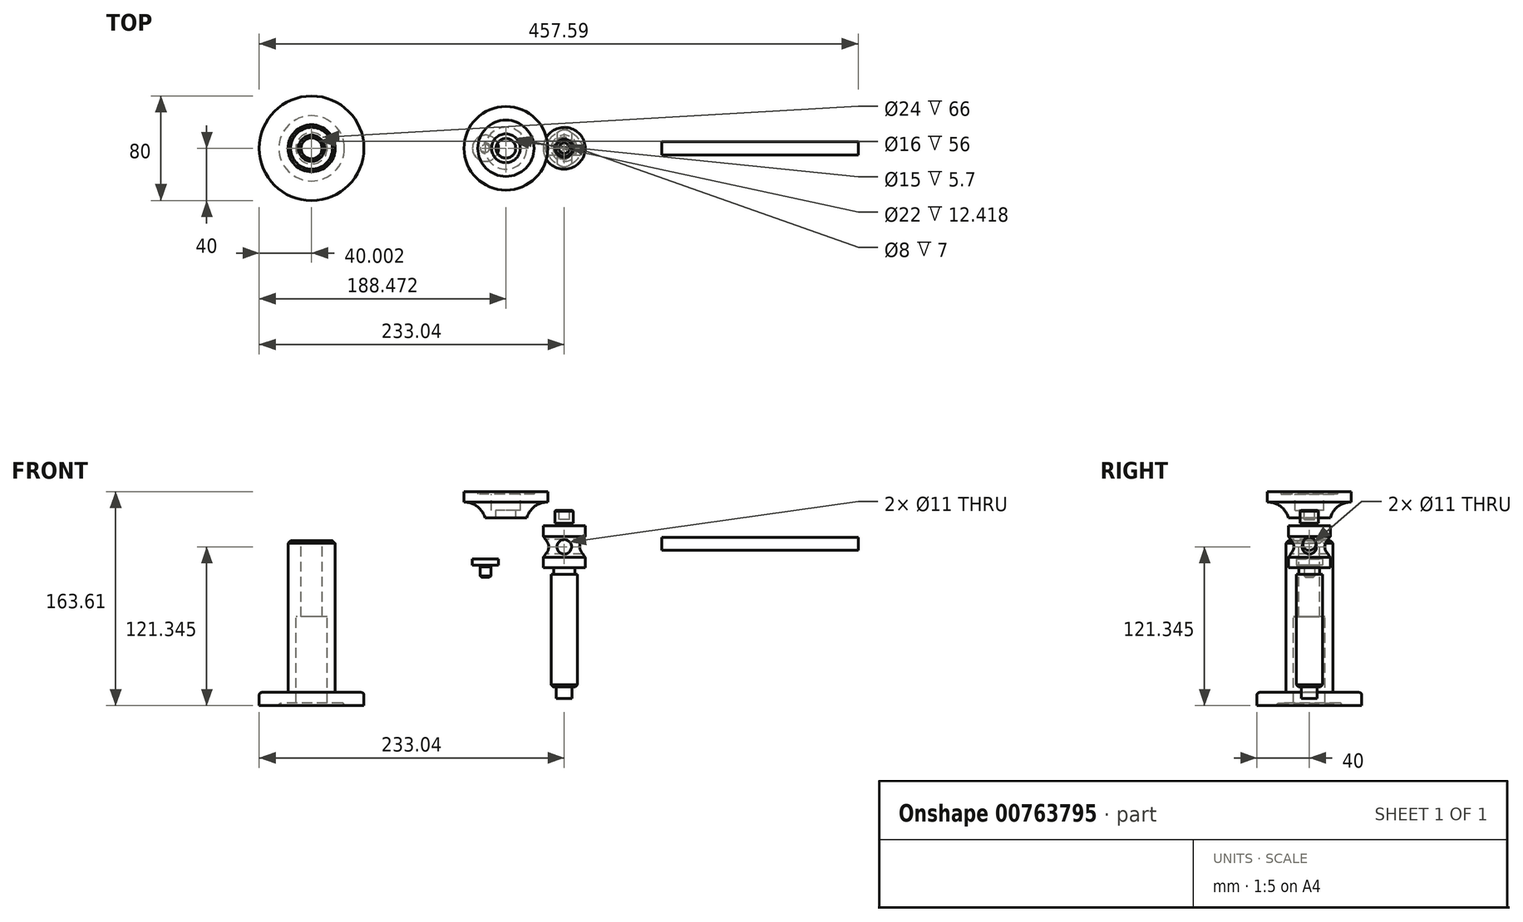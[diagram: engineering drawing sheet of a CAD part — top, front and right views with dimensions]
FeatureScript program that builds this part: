
annotation { "Feature Type Name" : "Feature", "Feature Type Description" : "" }
export const myFeature = defineFeature(function(context is Context, id is Id, definition is map)
    precondition{}
    {
        {
            var Q0;
            Q0=qCreatedBy(makeId("Right.planeOp"),FACE);
            var sketch = newSketch(context, id + "F0", { "sketchPlane" : qUnion([Q0])});
            skLineSegment(sketch, "E0", {"start": v(0, 128.7) * mm, "end": v(0, -124.16) * mm, "construction": true});
            skLineSegment(sketch, "E1", {"start": v(55.08, 81.35) * mm, "end": v(7, 81.35) * mm, "construction": true});
            skLineSegment(sketch, "E2", {"start": v(60.93, -62.65) * mm, "end": v(-52.02, -62.65) * mm, "construction": true});
            skLineSegment(sketch, "E3", {"start": v(58.64, 37.35) * mm, "end": v(-57.7, 37.35) * mm, "construction": true});
            skLineSegment(sketch, "E4", {"start": v(0, -62.65) * mm, "end": v(6, -62.65) * mm});
            skLineSegment(sketch, "E5", {"start": v(6, -62.65) * mm, "end": v(6, -53.65) * mm});
            skLineSegment(sketch, "E6", {"start": v(6, -53.65) * mm, "end": v(8.5, -53.65) * mm});
            skLineSegment(sketch, "E7", {"start": v(10, -52.15) * mm, "end": v(10, 32.35) * mm});
            skLineSegment(sketch, "E8", {"start": v(10, -52.15) * mm, "end": v(8.5, -53.65) * mm});
            skPoint(sketch, "E9.orphan", {"position": v(10, -53.65) * mm});
            skLineSegment(sketch, "E10", {"start": v(10, 32.35) * mm, "end": v(8, 32.35) * mm});
            skLineSegment(sketch, "E11", {"start": v(8, 32.35) * mm, "end": v(8, 37.35) * mm});
            skLineSegment(sketch, "E12", {"start": v(8, 37.35) * mm, "end": v(16, 37.35) * mm});
            skLineSegment(sketch, "E13", {"start": v(16, 37.35) * mm, "end": v(16, 45.4) * mm});
            skLineSegment(sketch, "E14", {"start": v(32.6, 53.35) * mm, "end": v(-18.75, 53.35) * mm, "construction": true});
            skLineSegment(sketch, "E15", {"start": v(0, -62.65) * mm, "end": v(0, 81.35) * mm});
            skLineSegment(sketch, "E16", {"start": v(16, 69.35) * mm, "end": v(6, 69.35) * mm});
            skLineSegment(sketch, "E17", {"start": v(7, 81.35) * mm, "end": v(0, 81.35) * mm});
            skLineSegment(sketch, "E18", {"start": v(6.98, 71.36) * mm, "end": v(7, 80.73) * mm});
            skLineSegment(sketch, "E19.0", {"start": v(6, 69.35) * mm, "end": v(6, 71.35) * mm});
            skLineSegment(sketch, "E20", {"start": v(6.98, 71.36) * mm, "end": v(6, 71.35) * mm});
            skLineSegment(sketch, "E21", {"start": v(6.3, 81.35) * mm, "end": v(7, 80.73) * mm});
            skLineSegment(sketch, "E22.trimOffspring", {"start": v(6.3, 81.35) * mm, "end": v(-42.12, 81.35) * mm, "construction": true});
            skArc(sketch, "E23", {"start": v(16, 61.28) * mm, "mid": v(13, 53.35) * mm, "end": v(16, 45.4) * mm});
            skLineSegment(sketch, "E24.trimOffspring", {"start": v(16, 61.28) * mm, "end": v(16, 69.35) * mm});
            skSolve(sketch);
        }
        {
            var Q0;
            Q0=makeQuery(id+"F0.imprint","IMPRINT",FACE,{"disambiguationData":[TD([[makeQuery(id+"F0.imprint","IMPRINT",EDGE,{"derivedFrom":sQuery(id+"F0.wireOp",EDGE,"E4")}),1.0]])]});
            var Q1;
            Q1=sQuery(id+"F0.wireOp",EDGE,"E15");
            revolve(context, id + "F1", {"surfaceOperationType" : NewSurfaceOperationType.NEW, "entities" : qUnion([Q0]), "axis" : qUnion([Q1]), "revolveType" : RevolveType.FULL});
        }
        {
            var Q0;
            Q0=qCreatedBy(makeId("Front.planeOp"),FACE);
            var sketch = newSketch(context, id + "F2", { "sketchPlane" : qUnion([Q0])});
            skCircle(sketch, "E25", {"center": v(0, 53.35) * mm, "radius": 5.5 * mm});
            skSolve(sketch);
        }
        {
            var Q0;
            Q0 = qSketchRegion(id + "F2", true);
            extrude(context, id + "F3", {"entities" : qUnion([Q0]), "operationType" : NewBodyOperationType.REMOVE, "oppositeDirection" : true, "depth" : 25.4 * mm, "offsetDistance" : 25.4 * mm, "hasSecondDirection" : true, "secondDirectionOppositeDirection" : false, "secondDirectionDepth" : 25.4 * mm});
        }
        {
            var Q0;
            Q0=qCreatedBy(makeId("Right.planeOp"),FACE);
            var sketch = newSketch(context, id + "F4", { "sketchPlane" : qUnion([Q0])});
            skCircle(sketch, "E26", {"center": v(0, 53.35) * mm, "radius": 5.5 * mm});
            skSolve(sketch);
        }
        {
            var Q0;
            Q0 = qSketchRegion(id + "F4", true);
            extrude(context, id + "F5", {"entities" : qUnion([Q0]), "operationType" : NewBodyOperationType.REMOVE, "depth" : 25.4 * mm, "offsetDistance" : 25.4 * mm, "hasSecondDirection" : true, "secondDirectionOppositeDirection" : true, "secondDirectionDepth" : 25.4 * mm});
        }
        {
            var Q0;
            Q0=qCreatedBy(makeId("Front.planeOp"),FACE);
            var sketch = newSketch(context, id + "F6", { "sketchPlane" : qUnion([Q0])});
            skLineSegment(sketch, "E27", {"start": v(74.55, 55.62) * mm, "end": v(224.55, 55.62) * mm});
            skLineSegment(sketch, "E28", {"start": v(224.55, 55.62) * mm, "end": v(224.55, 60.62) * mm});
            skLineSegment(sketch, "E29", {"start": v(224.55, 60.62) * mm, "end": v(74.55, 60.62) * mm});
            skLineSegment(sketch, "E30", {"start": v(74.55, 60.62) * mm, "end": v(74.55, 55.62) * mm});
            skSolve(sketch);
        }
        {
            var Q0;
            Q0 = qSketchRegion(id + "F6", true);
            var Q1;
            Q1=sQuery(id+"F6.wireOp",EDGE,"E27");
            revolve(context, id + "F7", {"surfaceOperationType" : NewSurfaceOperationType.NEW, "entities" : qUnion([Q0]), "axis" : qUnion([Q1]), "revolveType" : RevolveType.FULL});
        }
        {
            var Q0;
            Q0=qCreatedBy(makeId("Front.planeOp"),FACE);
            var sketch = newSketch(context, id + "F8", { "sketchPlane" : qUnion([Q0])});
            skLineSegment(sketch, "E31", {"start": v(-60.15, 44.19) * mm, "end": v(-50.15, 44.19) * mm});
            skLineSegment(sketch, "E32", {"start": v(-50.15, 44.19) * mm, "end": v(-50.15, 39.19) * mm});
            skLineSegment(sketch, "E33", {"start": v(-50.15, 39.19) * mm, "end": v(-57.15, 39.19) * mm});
            skLineSegment(sketch, "E34", {"start": v(-57.15, 39.19) * mm, "end": v(-57.15, 38.19) * mm});
            skLineSegment(sketch, "E35", {"start": v(-56.15, 38.19) * mm, "end": v(-56.15, 31.19) * mm});
            skLineSegment(sketch, "E36", {"start": v(-57.15, 30.19) * mm, "end": v(-60.15, 30.19) * mm});
            skLineSegment(sketch, "E37", {"start": v(-60.15, 30.19) * mm, "end": v(-60.15, 44.19) * mm});
            skLineSegment(sketch, "E38", {"start": v(-57.15, 38.19) * mm, "end": v(-56.15, 38.19) * mm});
            skLineSegment(sketch, "E39", {"start": v(-57.15, 30.19) * mm, "end": v(-56.15, 31.19) * mm});
            skPoint(sketch, "E40.orphan", {"position": v(-56.15, 30.19) * mm});
            skSolve(sketch);
        }
        {
            var Q0;
            Q0 = qSketchRegion(id + "F8", true);
            var Q1;
            Q1=sQuery(id+"F8.wireOp",EDGE,"E37");
            revolve(context, id + "F9", {"surfaceOperationType" : NewSurfaceOperationType.NEW, "entities" : qUnion([Q0]), "axis" : qUnion([Q1]), "revolveType" : RevolveType.FULL});
        }
        {
            var Q0;
            Q0=qCreatedBy(makeId("Front.planeOp"),FACE);
            var sketch = newSketch(context, id + "F10", { "sketchPlane" : qUnion([Q0])});
            skLineSegment(sketch, "E41", {"start": v(-23.07, 95.6) * mm, "end": v(-12.57, 95.6) * mm});
            skLineSegment(sketch, "E42", {"start": v(-28.57, 75.6) * mm, "end": v(-37.07, 75.6) * mm});
            skLineSegment(sketch, "E43", {"start": v(-12.57, 87.6) * mm, "end": v(-12.57, 95.6) * mm});
            skLineSegment(sketch, "E44", {"start": v(-37.07, 75.6) * mm, "end": v(-37.07, 81.3) * mm});
            skLineSegment(sketch, "E45", {"start": v(-37.07, 81.3) * mm, "end": v(-33.57, 81.3) * mm});
            skLineSegment(sketch, "E46", {"start": v(-33.57, 81.3) * mm, "end": v(-33.57, 93.72) * mm});
            skLineSegment(sketch, "E47", {"start": v(-33.57, 93.72) * mm, "end": v(-22.96, 93.72) * mm});
            skLineSegment(sketch, "E48", {"start": v(-22.96, 93.72) * mm, "end": v(-23.07, 95.6) * mm});
            skLineSegment(sketch, "E49", {"start": v(-44.57, 91.35) * mm, "end": v(-44.57, 69.07) * mm, "construction": true});
            skArc(sketch, "E50", {"start": v(-12.57, 87.6) * mm, "mid": v(-22.57, 84.27) * mm, "end": v(-28.57, 75.6) * mm});
            skSolve(sketch);
        }
        {
            var Q0;
            Q0 = qSketchRegion(id + "F10", true);
            var Q1;
            Q1=sQuery(id+"F10.wireOp",EDGE,"E49");
            revolve(context, id + "F11", {"surfaceOperationType" : NewSurfaceOperationType.NEW, "entities" : qUnion([Q0]), "axis" : qUnion([Q1]), "revolveType" : RevolveType.FULL});
        }
        {
            var Q0;
            Q0=makeQuery(id+"F1.opRevolve","SWEPT_FACE",FACE,{"disambiguationData":[OSD([sQuery(id+"F0.wireOp",EDGE,"E17")])]});
            var sketch = newSketch(context, id + "F12", { "sketchPlane" : qUnion([Q0])});
            skCircle(sketch, "E51", {"center": v(0, 0) * mm, "radius": 4 * mm});
            skSolve(sketch);
        }
        {
            var Q0;
            Q0 = qSketchRegion(id + "F12", true);
            extrude(context, id + "F13", {"entities" : qUnion([Q0]), "operationType" : NewBodyOperationType.REMOVE, "oppositeDirection" : true, "depth" : 7 * mm, "offsetDistance" : 25 * mm});
        }
        {
            var Q0;
            Q0=qCreatedBy(makeId("Front.planeOp"),FACE);
            var sketch = newSketch(context, id + "F14", { "sketchPlane" : qUnion([Q0])});
            skLineSegment(sketch, "E52", {"start": v(-175.04, 56) * mm, "end": v(-175.04, -58) * mm});
            skLineSegment(sketch, "E53", {"start": v(-175.04, -58) * mm, "end": v(-155.04, -58) * mm});
            skLineSegment(sketch, "E54", {"start": v(-153.04, -60) * mm, "end": v(-153.04, -68) * mm});
            skLineSegment(sketch, "E55", {"start": v(-153.04, -68) * mm, "end": v(-168.04, -68) * mm});
            skLineSegment(sketch, "E56", {"start": v(-168.04, -68) * mm, "end": v(-168.04, -68) * mm});
            skLineSegment(sketch, "E57", {"start": v(-170.04, -66) * mm, "end": v(-181.04, -66) * mm});
            skLineSegment(sketch, "E58", {"start": v(-181.04, -66) * mm, "end": v(-181.04, 0) * mm});
            skLineSegment(sketch, "E59", {"start": v(-181.04, 0) * mm, "end": v(-185.04, 0) * mm});
            skLineSegment(sketch, "E60", {"start": v(-185.04, 0) * mm, "end": v(-185.04, 56) * mm});
            skLineSegment(sketch, "E61", {"start": v(-193.04, 52.28) * mm, "end": v(-193.04, -98.03) * mm, "construction": true});
            skLineSegment(sketch, "E62", {"start": v(-177.04, 58) * mm, "end": v(-175.04, 56) * mm});
            skPoint(sketch, "E63.orphan", {"position": v(-175.04, 58) * mm});
            skLineSegment(sketch, "E64", {"start": v(-183.04, 58) * mm, "end": v(-177.04, 58) * mm});
            skLineSegment(sketch, "E65", {"start": v(-183.04, 58) * mm, "end": v(-185.04, 56) * mm});
            skPoint(sketch, "E66.visualSharp", {"position": v(-168.04, -66) * mm});
            skArc(sketch, "E66.filletArc", {"start": v(-168.04, -68) * mm, "mid": v(-168.62, -66.59) * mm, "end": v(-170.04, -66) * mm});
            skPoint(sketch, "E67.visualSharp", {"position": v(-153.04, -58) * mm});
            skArc(sketch, "E67.filletArc", {"start": v(-153.04, -60) * mm, "mid": v(-153.62, -58.59) * mm, "end": v(-155.04, -58) * mm});
            skSolve(sketch);
        }
        {
            var Q0;
            Q0 = qSketchRegion(id + "F14", true);
            var Q1;
            Q1=sQuery(id+"F14.wireOp",EDGE,"E61");
            revolve(context, id + "F15", {"surfaceOperationType" : NewSurfaceOperationType.NEW, "entities" : qUnion([Q0]), "axis" : qUnion([Q1]), "revolveType" : RevolveType.FULL});
        }
    });
